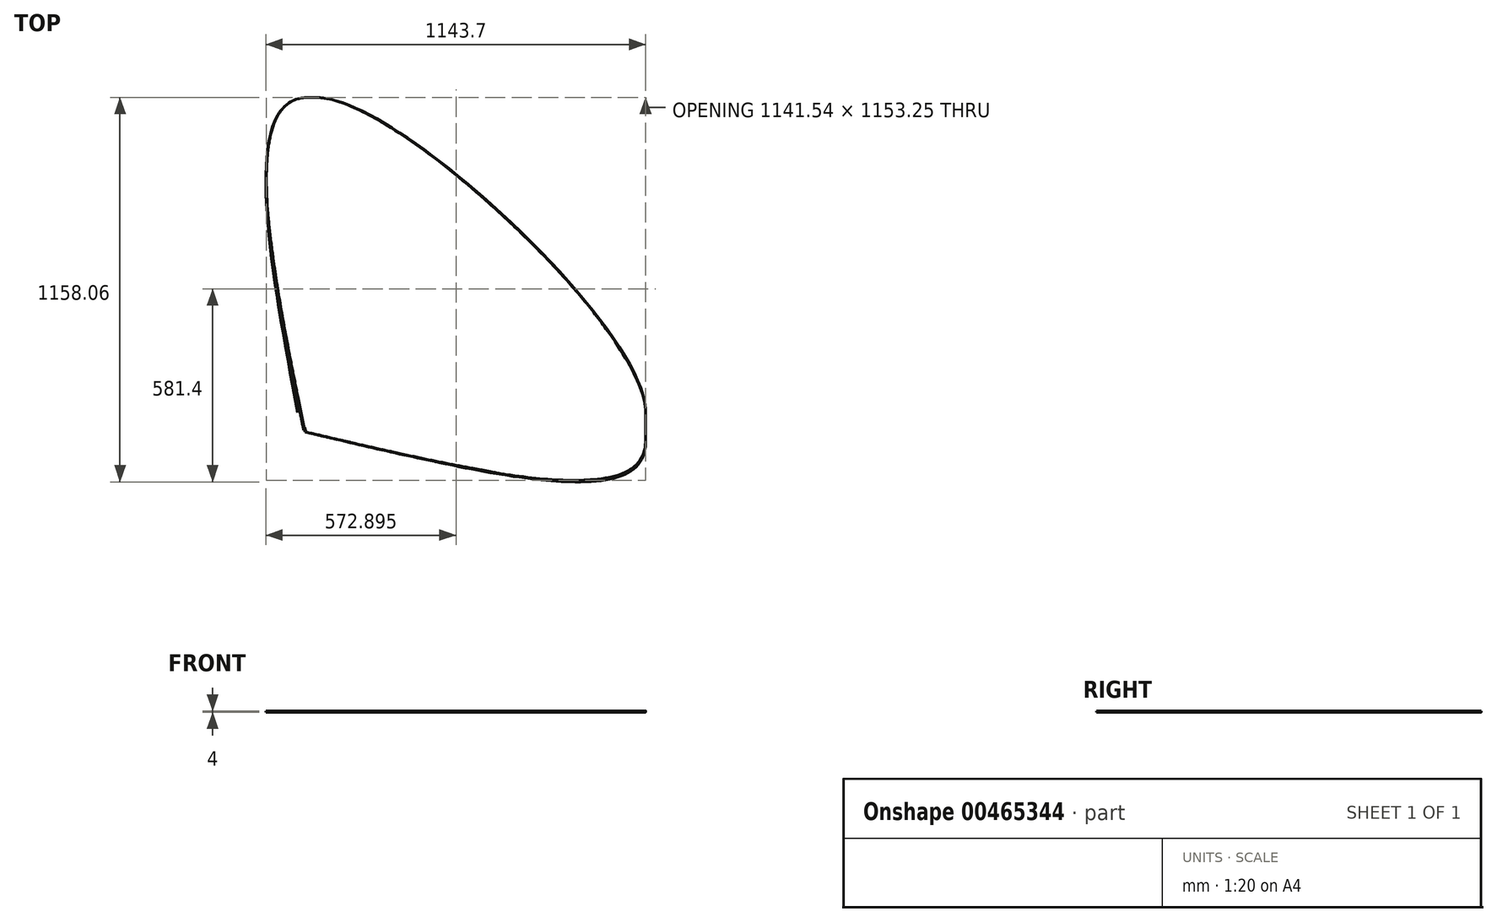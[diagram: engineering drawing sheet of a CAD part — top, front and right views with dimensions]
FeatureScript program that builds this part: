
annotation { "Feature Type Name" : "Feature", "Feature Type Description" : "" }
export const myFeature = defineFeature(function(context is Context, id is Id, definition is map)
    precondition{}
    {
        {
            var Q0;
            Q0=qCreatedBy(makeId("Top.planeOp"),FACE);
            var sketch = newSketch(context, id + "F0", { "sketchPlane" : qUnion([Q0])});
            skLineSegment(sketch, "E0", {"start": v(-37.67, 6.7) * mm, "end": v(-36, 6.6) * mm});
            skLineSegment(sketch, "E1", {"start": v(-36, 6.6) * mm, "end": v(-36, -0.1) * mm});
            skLineSegment(sketch, "E2", {"start": v(-28.6, 14.4) * mm, "end": v(-29.98, 14.4) * mm});
            skLineSegment(sketch, "E3", {"start": v(-28.6, 9.42) * mm, "end": v(-28.6, 11.89) * mm});
            skLineSegment(sketch, "E4", {"start": v(-28.6, 11.89) * mm, "end": v(-28.6, 14.4) * mm});
            skLineSegment(sketch, "E5", {"start": v(-0.8, 6.21) * mm, "end": v(0.5, 6.1) * mm});
            skLineSegment(sketch, "E6", {"start": v(7.03, 4.1) * mm, "end": v(8.33, 5.22) * mm});
            skLineSegment(sketch, "E7", {"start": v(7.03, -1.97) * mm, "end": v(7.03, 4.1) * mm});
            skLineSegment(sketch, "E8", {"start": v(0.5, 6.1) * mm, "end": v(0.5, -0.6) * mm});
            skLineSegment(sketch, "E9", {"start": v(15.5, 3.5) * mm, "end": v(15.5, -1.9) * mm});
            skLineSegment(sketch, "E10", {"start": v(-22.25, 8.33) * mm, "end": v(-22.25, 9.63) * mm});
            skLineSegment(sketch, "E11", {"start": v(-28.6, 1.17) * mm, "end": v(-28.6, 6.99) * mm});
            skLineSegment(sketch, "E12", {"start": v(14.26, 4.76) * mm, "end": v(15.5, 3.5) * mm});
            skLineSegment(sketch, "E13", {"start": v(-22.25, 6.99) * mm, "end": v(-22.25, 8.33) * mm});
            skLineSegment(sketch, "E14", {"start": v(-28.6, 6.99) * mm, "end": v(-25.43, 6.99) * mm});
            skLineSegment(sketch, "E15", {"start": v(-25.43, 6.99) * mm, "end": v(-22.25, 6.99) * mm});
            skLineSegment(sketch, "E16", {"start": v(-25.43, 9.53) * mm, "end": v(-28.6, 9.42) * mm});
            skLineSegment(sketch, "E17", {"start": v(-15.65, 5.58) * mm, "end": v(-14.38, 6.8) * mm});
            skLineSegment(sketch, "E18", {"start": v(-14.88, 4.73) * mm, "end": v(-15.65, 5.58) * mm});
            skLineSegment(sketch, "E19", {"start": v(-22.25, 9.63) * mm, "end": v(-25.43, 9.53) * mm});
            skFitSpline(sketch, "E20", {"points": [v(-35.34, -8.15) * mm, v(1000, -34.07) * mm, v(-10.58, 1000) * mm, v(-30.12, -11.64) * mm]});
            skFitSpline(sketch, "E21", {"points": [v(-22.6, -7.65) * mm, v(1000, -22.6) * mm, v(-6.88, 1000) * mm, v(-22.67, -6.84) * mm]});
            skFitSpline(sketch, "E22", {"points": [v(-39.47, 7.59) * mm, v(1000, -39.36) * mm, v(6.92, 1000) * mm, v(-39.11, 6.8) * mm]});
            skFitSpline(sketch, "E23", {"points": [v(-26.38, -10.51) * mm, v(1000, -24.12) * mm, v(-9.84, 1000) * mm, v(-22.6, -8.68) * mm]});
            skFitSpline(sketch, "E24", {"points": [v(-23.7, -7.2) * mm, v(1000, -24.47) * mm, v(-7.48, 1000) * mm, v(-25.14, -7.44) * mm]});
            skFitSpline(sketch, "E25", {"points": [v(-36, -0.1) * mm, v(1000, -36) * mm, v(-6.03, 1000) * mm, v(-35.94, -6.95) * mm]});
            skFitSpline(sketch, "E26", {"points": [v(-26.17, -7.16) * mm, v(1000, -28.35) * mm, v(-6.49, 1000) * mm, v(-28.6, -5.68) * mm]});
            skFitSpline(sketch, "E27", {"points": [v(-1.05, 8.4) * mm, v(1000, -2.04) * mm, v(8.4, 1000) * mm, v(-2.14, 8.3) * mm]});
            skFitSpline(sketch, "E28", {"points": [v(-2.14, 7.37) * mm, v(1000, -2.14) * mm, v(6.42, 1000) * mm, v(-2.04, 6.32) * mm]});
            skFitSpline(sketch, "E29", {"points": [v(-36.43, 9.84) * mm, v(1000, -39.15) * mm, v(8.57, 1000) * mm, v(-39.57, 8.3) * mm]});
            skFitSpline(sketch, "E30", {"points": [v(11.33, 6.21) * mm, v(1000, 12.7) * mm, v(6.07, 1000) * mm, v(13.27, 5.79) * mm]});
            skFitSpline(sketch, "E31", {"points": [v(4.03, 9.88) * mm, v(1000, 2.69) * mm, v(9.07, 1000) * mm, v(0.36, 8.4) * mm]});
            skFitSpline(sketch, "E32", {"points": [v(-29.98, 14.4) * mm, v(1000, -31.18) * mm, v(14.4, 1000) * mm, v(-31.42, 14.25) * mm]});
            skFitSpline(sketch, "E33", {"points": [v(8.33, 5.22) * mm, v(1000, 9.5) * mm, v(6.25, 1000) * mm, v(9.78, 6.35) * mm]});
            skFitSpline(sketch, "E34", {"points": [v(9.57, -10.16) * mm, v(1000, 7.24) * mm, v(-9.35, 1000) * mm, v(7.03, -8.71) * mm]});
            skFitSpline(sketch, "E35", {"points": [v(3.92, -10.62) * mm, v(1000, 9.67) * mm, v(-10.62, 1000) * mm, v(10.56, -10.55) * mm]});
            skFitSpline(sketch, "E36", {"points": [v(-1.5, -9.84) * mm, v(1000, -4.19) * mm, v(-10.37, 1000) * mm, v(-2.28, -10.65) * mm]});
            skFitSpline(sketch, "E37", {"points": [v(0.5, -0.6) * mm, v(1000, 0.5) * mm, v(-8.22, 1000) * mm, v(0.22, -9.49) * mm]});
            skFitSpline(sketch, "E38", {"points": [v(-17.63, -5.57) * mm, v(1000, -18.48) * mm, v(-4.7, 1000) * mm, v(-19.18, -4.3) * mm]});
            skFitSpline(sketch, "E39", {"points": [v(-12.16, -8.18) * mm, v(1000, -14.14) * mm, v(-8.18, 1000) * mm, v(-15.97, -7.3) * mm]});
            skFitSpline(sketch, "E40", {"points": [v(-7.96, -6.53) * mm, v(1000, -8.32) * mm, v(-7.37, 1000) * mm, v(-10.36, -8.18) * mm]});
            skFitSpline(sketch, "E41", {"points": [v(-11.03, -3.39) * mm, v(1000, -9.1) * mm, v(-4.34, 1000) * mm, v(-7.68, -5.78) * mm]});
            skFitSpline(sketch, "E42", {"points": [v(-14.67, 9.7) * mm, v(1000, -18.4) * mm, v(8.82, 1000) * mm, v(-20.49, 6.8) * mm]});
            skFitSpline(sketch, "E43", {"points": [v(-15.65, -1.1) * mm, v(1000, -13.96) * mm, v(-1.94, 1000) * mm, v(-11.88, -2.96) * mm]});
            skFitSpline(sketch, "E44", {"points": [v(-20.49, 4.16) * mm, v(1000, -20.49) * mm, v(1.9, 1000) * mm, v(-19.4, 0.7) * mm]});
            skFitSpline(sketch, "E45", {"points": [v(6.08, 10.51) * mm, v(1000, 5.51) * mm, v(10.51, 1000) * mm, v(4.63, 10.23) * mm]});
            skFitSpline(sketch, "E46", {"points": [v(7.03, 8.93) * mm, v(1000, 7.03) * mm, v(10.4, 1000) * mm, v(6.96, 10.51) * mm]});
            skFitSpline(sketch, "E47", {"points": [v(10.56, 8.4) * mm, v(1000, 7.13) * mm, v(6.99, 1000) * mm, v(7.03, 7.02) * mm]});
            skFitSpline(sketch, "E48", {"points": [v(15.74, 9.46) * mm, v(1000, 13.63) * mm, v(9.46, 1000) * mm, v(12.6, 9.24) * mm]});
            skFitSpline(sketch, "E49", {"points": [v(21.03, 7.59) * mm, v(1000, 19.27) * mm, v(9.14, 1000) * mm, v(18.39, 9.46) * mm]});
            skFitSpline(sketch, "E50", {"points": [v(-19.85, -4.3) * mm, v(1000, -20.95) * mm, v(-4.3, 1000) * mm, v(-20.98, -4.48) * mm]});
            skFitSpline(sketch, "E51", {"points": [v(-20, -9.2) * mm, v(1000, -19.89) * mm, v(-9.98, 1000) * mm, v(-19.68, -10.09) * mm]});
            skFitSpline(sketch, "E52", {"points": [v(-4.75, -9.42) * mm, v(1000, -4.47) * mm, v(-9.14, 1000) * mm, v(-4.05, -8.78) * mm]});
            skFitSpline(sketch, "E53", {"points": [v(-6.8, -10.2) * mm, v(1000, -5.95) * mm, v(-10.05, 1000) * mm, v(-5.04, -9.7) * mm]});
            skFitSpline(sketch, "E54", {"points": [v(-17.8, -10.26) * mm, v(1000, -14.77) * mm, v(-10.51, 1000) * mm, v(-8.56, -10.51) * mm]});
            skFitSpline(sketch, "E55", {"points": [v(-20.45, -6.77) * mm, v(1000, -20.24) * mm, v(-7.65, 1000) * mm, v(-20.03, -8.75) * mm]});
            skFitSpline(sketch, "E56", {"points": [v(21.5, -1.8) * mm, v(1000, 21.5) * mm, v(3.99, 1000) * mm, v(21.78, 4.83) * mm]});
            skFitSpline(sketch, "E57", {"points": [v(-32.3, 12.84) * mm, v(1000, -33.15) * mm, v(11.5, 1000) * mm, v(-33.75, 11.04) * mm]});
            skFitSpline(sketch, "E58", {"points": [v(28.44, -10.09) * mm, v(1000, 27.42) * mm, v(-10.55, 1000) * mm, v(27.88, -10.58) * mm]});
            skFitSpline(sketch, "E59", {"points": [v(13.48, -9.88) * mm, v(1000, 13.03) * mm, v(-9.95, 1000) * mm, v(12.67, -10.16) * mm]});
            skFitSpline(sketch, "E60", {"points": [v(23.75, -10.12) * mm, v(1000, 21.95) * mm, v(-9.31, 1000) * mm, v(21.5, -7.62) * mm]});
            skFitSpline(sketch, "E61", {"points": [v(15.5, -1.9) * mm, v(1000, 15.5) * mm, v(-7.87, 1000) * mm, v(15.04, -9.66) * mm]});
            skFitSpline(sketch, "E62", {"points": [v(38.36, -10.12) * mm, v(1000, 36.98) * mm, v(-9.35, 1000) * mm, v(36.66, -7.76) * mm]});
            skFitSpline(sketch, "E63", {"points": [v(18.78, -10.62) * mm, v(1000, 24.2) * mm, v(-10.58, 1000) * mm, v(24.74, -10.55) * mm]});
            skFitSpline(sketch, "E64", {"points": [v(23.96, 5.72) * mm, v(1000, 25.8) * mm, v(6.46, 1000) * mm, v(27.07, 6.42) * mm]});
            skFitSpline(sketch, "E65", {"points": [v(28.3, 5.65) * mm, v(1000, 30.2) * mm, v(4.38, 1000) * mm, v(30.28, 4.06) * mm]});
            skFitSpline(sketch, "E66", {"points": [v(12.67, -10.34) * mm, v(1000, 12.67) * mm, v(-10.51, 1000) * mm, v(15.21, -10.65) * mm]});
            skFitSpline(sketch, "E67", {"points": [v(36.66, -1.13) * mm, v(1000, 36.63) * mm, v(5.61, 1000) * mm, v(36.2, 7.3) * mm]});
            skFitSpline(sketch, "E68", {"points": [v(34.23, 8.64) * mm, v(1000, 33.24) * mm, v(9.31, 1000) * mm, v(32.53, 9.46) * mm]});
            skFitSpline(sketch, "E69", {"points": [v(30.49, 9.46) * mm, v(1000, 28.34) * mm, v(9.46, 1000) * mm, v(27.42, 9.24) * mm]});
            skFitSpline(sketch, "E70", {"points": [v(24.84, 8.19) * mm, v(1000, 21.81) * mm, v(6.92, 1000) * mm, v(21.81, 6.92) * mm]});
            skFitSpline(sketch, "E71", {"points": [v(54.27, 5.79) * mm, v(1000, 55.43) * mm, v(4.1, 1000) * mm, v(57.3, 2.4) * mm]});
            skFitSpline(sketch, "E72", {"points": [v(45.83, -10.3) * mm, v(1000, 48.3) * mm, v(-11.08, 1000) * mm, v(52.57, -11.25) * mm]});
            skFitSpline(sketch, "E73", {"points": [v(-9.55, 6.67) * mm, v(1000, -9.45) * mm, v(6.53, 1000) * mm, v(-8.81, 6.03) * mm]});
            skFitSpline(sketch, "E74", {"points": [v(-7.26, 9.6) * mm, v(1000, -8.42) * mm, v(9.67, 1000) * mm, v(-10.15, 9.8) * mm]});
            skFitSpline(sketch, "E75", {"points": [v(-14.38, 6.8) * mm, v(1000, -13.68) * mm, v(7.52, 1000) * mm, v(-12.76, 8.04) * mm]});
            skFitSpline(sketch, "E76", {"points": [v(-4.61, 3.63) * mm, v(1000, -3.7) * mm, v(3.85, 1000) * mm, v(-3.59, 3.99) * mm]});
            skFitSpline(sketch, "E77", {"points": [v(-3.8, -8.64) * mm, v(1000, -2.99) * mm, v(-8.11, 1000) * mm, v(-2.14, -6.45) * mm]});
            skFitSpline(sketch, "E78", {"points": [v(-6.24, 3.95) * mm, v(1000, -5.85) * mm, v(3.56, 1000) * mm, v(-5.35, 3.46) * mm]});
            skFitSpline(sketch, "E79", {"points": [v(49.82, -6.24) * mm, v(1000, 46.12) * mm, v(-5.18, 1000) * mm, v(44.42, -3.07) * mm]});
            skFitSpline(sketch, "E80", {"points": [v(58.85, 8.43) * mm, v(1000, 56.45) * mm, v(9.63, 1000) * mm, v(51.16, 10.13) * mm]});
            skFitSpline(sketch, "E81", {"points": [v(61.32, -6.1) * mm, v(1000, 62.77) * mm, v(-4.1, 1000) * mm, v(61.74, -2.79) * mm]});
            skFitSpline(sketch, "E82", {"points": [v(-11.14, 9.91) * mm, v(1000, -12.1) * mm, v(10.02, 1000) * mm, v(-13.68, 9.91) * mm]});
            skFitSpline(sketch, "E83", {"points": [v(60.02, -4.4) * mm, v(1000, 57.37) * mm, v(-6.88, 1000) * mm, v(54.12, -7.48) * mm]});
            skFitSpline(sketch, "E84", {"points": [v(54.2, -10.62) * mm, v(1000, 54.72) * mm, v(-10.4, 1000) * mm, v(55.47, -10.2) * mm]});
            skFitSpline(sketch, "E85", {"points": [v(38.88, -4.2) * mm, v(1000, 39.45) * mm, v(-6.45, 1000) * mm, v(42.7, -9.28) * mm]});
            skFitSpline(sketch, "E86", {"points": [v(-4.5, -0.92) * mm, v(1000, -5.88) * mm, v(0.1, 1000) * mm, v(-9.45, 2.05) * mm]});
            skFitSpline(sketch, "E87", {"points": [v(-9.9, 2.05) * mm, v(1000, -10.65) * mm, v(2.05, 1000) * mm, v(-14.1, 3.92) * mm]});
            skFitSpline(sketch, "E88", {"points": [v(-5.07, 9.39) * mm, v(1000, -5.1) * mm, v(9.46, 1000) * mm, v(-6.1, 9.56) * mm]});
            skFitSpline(sketch, "E89", {"points": [v(47.67, 9.42) * mm, v(1000, 40.93) * mm, v(8.12, 1000) * mm, v(37.3, 2.47) * mm]});
            skFitSpline(sketch, "E90", {"points": [v(-3.77, 4.8) * mm, v(1000, -4.05) * mm, v(5.96, 1000) * mm, v(-4.97, 9.24) * mm]});
            skFitSpline(sketch, "E91", {"points": [v(55.78, -10.12) * mm, v(1000, 56.8) * mm, v(-9.91, 1000) * mm, v(60.55, -7.2) * mm]});
            skFitSpline(sketch, "E92", {"points": [v(-2.14, -5.36) * mm, v(1000, -2.14) * mm, v(-3.91, 1000) * mm, v(-3.24, -1.83) * mm]});
            skFitSpline(sketch, "E93", {"points": [v(50, 7.34) * mm, v(1000, 52) * mm, v(7.97, 1000) * mm, v(53.03, 7.59) * mm]});
            skFitSpline(sketch, "E94", {"points": [v(44.42, 0.57) * mm, v(1000, 44.42) * mm, v(3.78, 1000) * mm, v(46.5, 6.32) * mm]});
            skFitSpline(sketch, "E95", {"points": [v(57.93, 2.4) * mm, v(1000, 58.89) * mm, v(2.4, 1000) * mm, v(61, 3.18) * mm]});
            skFitSpline(sketch, "E96", {"points": [v(-8.07, 5.5) * mm, v(1000, -7.36) * mm, v(4.98, 1000) * mm, v(-6.55, 4.27) * mm]});
            skFitSpline(sketch, "E97", {"points": [v(-12.3, 8.04) * mm, v(1000, -11.6) * mm, v(8.04, 1000) * mm, v(-10.12, 7.3) * mm]});
            skFitSpline(sketch, "E98", {"points": [v(61.53, 3.7) * mm, v(1000, 62.66) * mm, v(4.83, 1000) * mm, v(61.36, 7.13) * mm]});
            skFitSpline(sketch, "E99", {"points": [v(33.31, -10.62) * mm, v(1000, 38.78) * mm, v(-10.62, 1000) * mm, v(39.24, -10.58) * mm]});
            skFitSpline(sketch, "E100", {"points": [v(30.31, -1.66) * mm, v(1000, 30.31) * mm, v(-8.04, 1000) * mm, v(30, -9.42) * mm]});
            skSolve(sketch);
        }
        {
            var Q0;
            Q0 = qSketchRegion(id + "F0", true);
            extrude(context, id + "F1", {"entities" : qUnion([Q0]), "depth" : 4 * mm, "offsetDistance" : 25 * mm});
        }
    });
